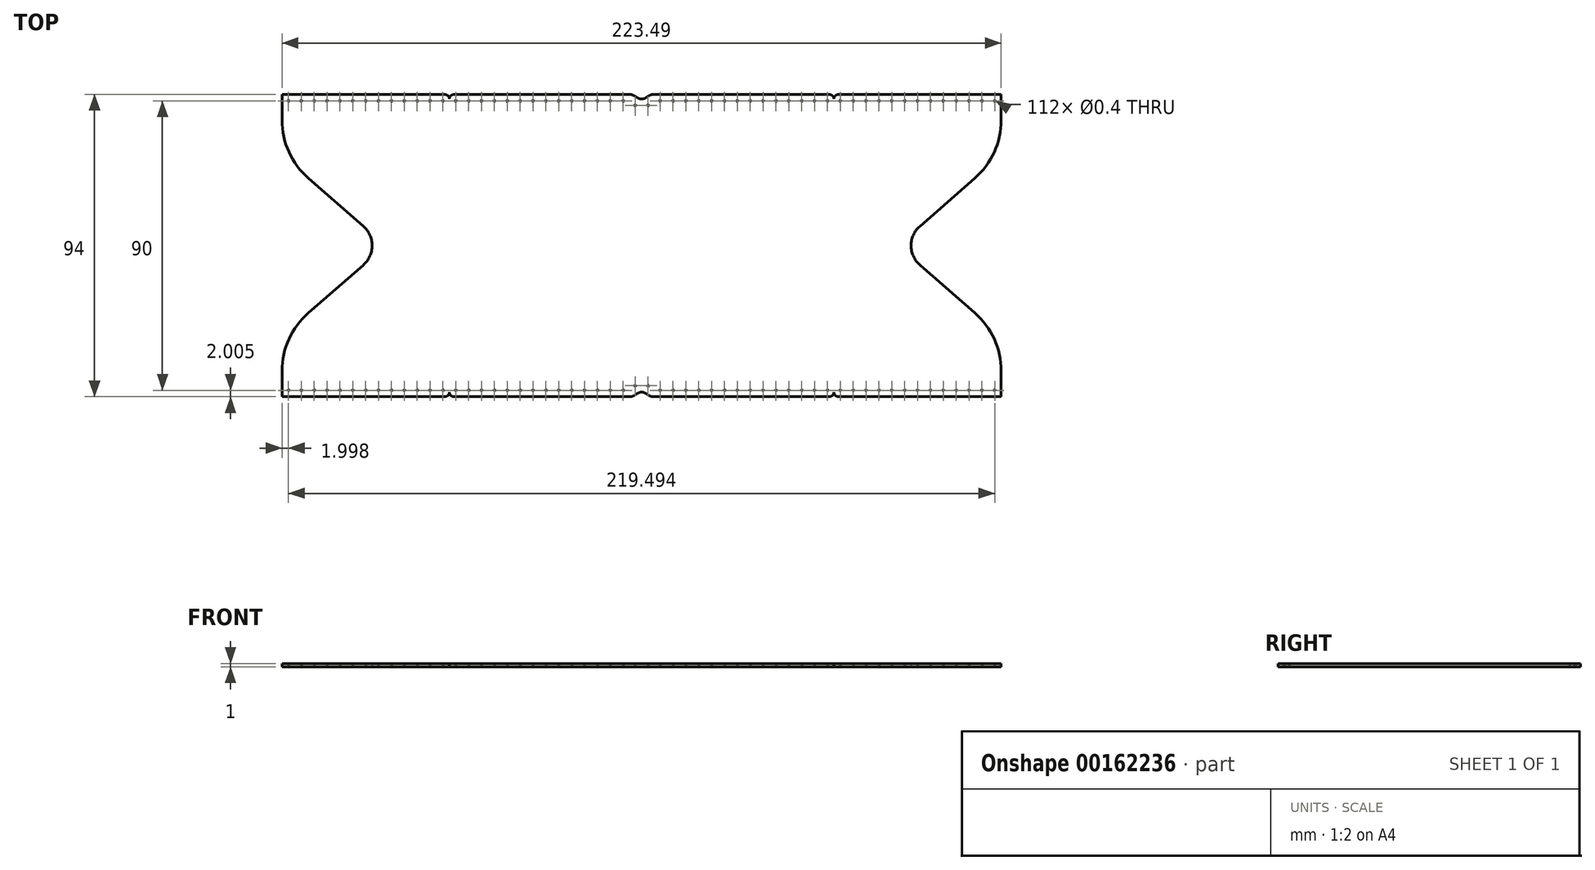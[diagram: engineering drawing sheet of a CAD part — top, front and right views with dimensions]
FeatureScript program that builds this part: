
annotation { "Feature Type Name" : "Feature", "Feature Type Description" : "" }
export const myFeature = defineFeature(function(context is Context, id is Id, definition is map)
    precondition{}
    {
        {
            var Q0;
            Q0=qCreatedBy(makeId("Top.planeOp"),FACE);
            var sketch = newSketch(context, id + "F0", { "sketchPlane" : qUnion([Q0])});
            skLineSegment(sketch, "E0", {"start": v(59.8, 51.12) * mm, "end": v(59.8, 5.52) * mm, "construction": true});
            skCircle(sketch, "E1.27.0.0", {"center": v(5.8, 50.52) * mm, "radius": 0.2 * mm});
            skLineSegment(sketch, "E2", {"start": v(86.53, 11.55) * mm, "end": v(103.58, 26.45) * mm});
            skArc(sketch, "E3", {"start": v(103.58, 26.45) * mm, "mid": v(109.64, 34.6) * mm, "end": v(111.8, 44.52) * mm});
            skArc(sketch, "E4", {"start": v(86.53, 11.55) * mm, "mid": v(84.5, 8.83) * mm, "end": v(83.8, 5.52) * mm});
            skLineSegment(sketch, "E5.trimOffspring", {"start": v(111.8, 44.52) * mm, "end": v(111.8, 52.52) * mm});
            skLineSegment(sketch, "E6.trimOffspring", {"start": v(3.65, 52.52) * mm, "end": v(58.4, 52.52) * mm});
            skCircle(sketch, "E7.1.0.0", {"center": v(9.8, 50.52) * mm, "radius": 0.2 * mm});
            skCircle(sketch, "E7.2.0.0", {"center": v(13.8, 50.52) * mm, "radius": 0.2 * mm});
            skCircle(sketch, "E7.3.0.0", {"center": v(17.8, 50.52) * mm, "radius": 0.2 * mm});
            skCircle(sketch, "E7.4.0.0", {"center": v(21.8, 50.52) * mm, "radius": 0.2 * mm});
            skCircle(sketch, "E7.5.0.0", {"center": v(25.8, 50.52) * mm, "radius": 0.2 * mm});
            skCircle(sketch, "E7.6.0.0", {"center": v(29.8, 50.52) * mm, "radius": 0.2 * mm});
            skCircle(sketch, "E7.7.0.0", {"center": v(33.8, 50.52) * mm, "radius": 0.2 * mm});
            skCircle(sketch, "E7.8.0.0", {"center": v(37.8, 50.52) * mm, "radius": 0.2 * mm});
            skCircle(sketch, "E7.9.0.0", {"center": v(41.8, 50.52) * mm, "radius": 0.2 * mm});
            skCircle(sketch, "E7.10.0.0", {"center": v(45.8, 50.52) * mm, "radius": 0.2 * mm});
            skCircle(sketch, "E7.11.0.0", {"center": v(49.8, 50.52) * mm, "radius": 0.2 * mm});
            skCircle(sketch, "E7.12.0.0", {"center": v(53.8, 50.52) * mm, "radius": 0.2 * mm});
            skCircle(sketch, "E7.13.0.0", {"center": v(57.8, 50.52) * mm, "radius": 0.2 * mm});
            skCircle(sketch, "E7.14.0.0", {"center": v(61.8, 50.52) * mm, "radius": 0.2 * mm});
            skCircle(sketch, "E7.15.0.0", {"center": v(65.8, 50.52) * mm, "radius": 0.2 * mm});
            skCircle(sketch, "E7.16.0.0", {"center": v(69.8, 50.52) * mm, "radius": 0.2 * mm});
            skCircle(sketch, "E7.17.0.0", {"center": v(73.8, 50.52) * mm, "radius": 0.2 * mm});
            skCircle(sketch, "E7.18.0.0", {"center": v(77.8, 50.52) * mm, "radius": 0.2 * mm});
            skCircle(sketch, "E7.19.0.0", {"center": v(81.8, 50.52) * mm, "radius": 0.2 * mm});
            skCircle(sketch, "E7.20.0.0", {"center": v(85.8, 50.52) * mm, "radius": 0.2 * mm});
            skCircle(sketch, "E7.21.0.0", {"center": v(89.8, 50.52) * mm, "radius": 0.2 * mm});
            skCircle(sketch, "E7.22.0.0", {"center": v(93.8, 50.52) * mm, "radius": 0.2 * mm});
            skCircle(sketch, "E7.23.0.0", {"center": v(97.8, 50.52) * mm, "radius": 0.2 * mm});
            skCircle(sketch, "E7.24.0.0", {"center": v(101.8, 50.52) * mm, "radius": 0.2 * mm});
            skCircle(sketch, "E7.25.0.0", {"center": v(105.8, 50.52) * mm, "radius": 0.2 * mm});
            skCircle(sketch, "E7.26.0.0", {"center": v(109.8, 50.52) * mm, "radius": 0.2 * mm});
            skLineSegment(sketch, "E7.direction1", {"start": v(5.8, 50.52) * mm, "end": v(9.8, 50.52) * mm, "construction": true});
            skArc(sketch, "E8", {"start": v(59.8, 51.12) * mm, "mid": v(59.38, 52.11) * mm, "end": v(58.4, 52.52) * mm});
            skArc(sketch, "E9", {"start": v(59.8, 51.12) * mm, "mid": v(60.2, 52.11) * mm, "end": v(61.2, 52.52) * mm});
            skLineSegment(sketch, "E10.trimOffspring", {"start": v(61.2, 52.52) * mm, "end": v(111.8, 52.52) * mm});
            skCircle(sketch, "E11", {"center": v(2.05, 49.12) * mm, "radius": 0.2 * mm});
            skFitSpline(sketch, "E12", {"points": [v(3.65, 52.52) * mm, v(1.85, 51.82) * mm, v(0.05, 51.12) * mm], "startDerivative": vector(-4.8, 0) * mm, "endDerivative": vector(-4.8, 0) * mm});
            skLineSegment(sketch, "E13", {"start": v(0.05, 5.52) * mm, "end": v(91.8, 5.52) * mm, "construction": true});
            skLineSegment(sketch, "E14", {"start": v(0.05, 5.52) * mm, "end": v(0.05, 51.12) * mm, "construction": true});
            skLineSegment(sketch, "E15", {"start": v(2.85, 52.52) * mm, "end": v(3.65, 52.52) * mm, "construction": true});
            skLineSegment(sketch, "E16", {"start": v(0.85, 51.12) * mm, "end": v(0.05, 51.12) * mm, "construction": true});
            skLineSegment(sketch, "E17.MirrorCS", {"start": v(0.85, -40.08) * mm, "end": v(0.05, -40.08) * mm, "construction": true});
            skLineSegment(sketch, "E18.MirrorCS", {"start": v(2.85, -41.48) * mm, "end": v(3.65, -41.48) * mm, "construction": true});
            skFitSpline(sketch, "E19.MirrorCS", {"points": [v(3.65, -41.48) * mm, v(1.85, -40.78) * mm, v(0.05, -40.08) * mm], "startDerivative": vector(-4.8, 0) * mm, "endDerivative": vector(-4.8, 0) * mm});
            skCircle(sketch, "E20.MirrorC", {"center": v(2.05, -38.08) * mm, "radius": 0.2 * mm});
            skLineSegment(sketch, "E21.MirrorCS", {"start": v(61.2, -41.48) * mm, "end": v(111.8, -41.48) * mm});
            skArc(sketch, "E22.MirrorCS", {"start": v(59.8, -40.08) * mm, "mid": v(60.2, -41.07) * mm, "end": v(61.2, -41.48) * mm});
            skArc(sketch, "E23.MirrorCS", {"start": v(59.8, -40.08) * mm, "mid": v(59.38, -41.07) * mm, "end": v(58.4, -41.48) * mm});
            skLineSegment(sketch, "E24.MirrorCS", {"start": v(59.8, -40.08) * mm, "end": v(59.8, 5.52) * mm, "construction": true});
            skLineSegment(sketch, "E25.MirrorCS", {"start": v(5.8, -39.48) * mm, "end": v(9.8, -39.48) * mm, "construction": true});
            skCircle(sketch, "E26.MirrorC", {"center": v(109.8, -39.48) * mm, "radius": 0.2 * mm});
            skCircle(sketch, "E27.MirrorC", {"center": v(105.8, -39.48) * mm, "radius": 0.2 * mm});
            skCircle(sketch, "E28.MirrorC", {"center": v(101.8, -39.48) * mm, "radius": 0.2 * mm});
            skCircle(sketch, "E29.MirrorC", {"center": v(97.8, -39.48) * mm, "radius": 0.2 * mm});
            skCircle(sketch, "E30.MirrorC", {"center": v(93.8, -39.48) * mm, "radius": 0.2 * mm});
            skCircle(sketch, "E31.MirrorC", {"center": v(89.8, -39.48) * mm, "radius": 0.2 * mm});
            skCircle(sketch, "E32.MirrorC", {"center": v(85.8, -39.48) * mm, "radius": 0.2 * mm});
            skCircle(sketch, "E33.MirrorC", {"center": v(81.8, -39.48) * mm, "radius": 0.2 * mm});
            skCircle(sketch, "E34.MirrorC", {"center": v(77.8, -39.48) * mm, "radius": 0.2 * mm});
            skCircle(sketch, "E35.MirrorC", {"center": v(73.8, -39.48) * mm, "radius": 0.2 * mm});
            skCircle(sketch, "E36.MirrorC", {"center": v(69.8, -39.48) * mm, "radius": 0.2 * mm});
            skCircle(sketch, "E37.MirrorC", {"center": v(65.8, -39.48) * mm, "radius": 0.2 * mm});
            skCircle(sketch, "E38.MirrorC", {"center": v(61.8, -39.48) * mm, "radius": 0.2 * mm});
            skCircle(sketch, "E39.MirrorC", {"center": v(57.8, -39.48) * mm, "radius": 0.2 * mm});
            skCircle(sketch, "E40.MirrorC", {"center": v(53.8, -39.48) * mm, "radius": 0.2 * mm});
            skCircle(sketch, "E41.MirrorC", {"center": v(49.8, -39.48) * mm, "radius": 0.2 * mm});
            skCircle(sketch, "E42.MirrorC", {"center": v(45.8, -39.48) * mm, "radius": 0.2 * mm});
            skCircle(sketch, "E43.MirrorC", {"center": v(41.8, -39.48) * mm, "radius": 0.2 * mm});
            skCircle(sketch, "E44.MirrorC", {"center": v(37.8, -39.48) * mm, "radius": 0.2 * mm});
            skCircle(sketch, "E45.MirrorC", {"center": v(33.8, -39.48) * mm, "radius": 0.2 * mm});
            skCircle(sketch, "E46.MirrorC", {"center": v(29.8, -39.48) * mm, "radius": 0.2 * mm});
            skCircle(sketch, "E47.MirrorC", {"center": v(25.8, -39.48) * mm, "radius": 0.2 * mm});
            skCircle(sketch, "E48.MirrorC", {"center": v(21.8, -39.48) * mm, "radius": 0.2 * mm});
            skCircle(sketch, "E49.MirrorC", {"center": v(17.8, -39.48) * mm, "radius": 0.2 * mm});
            skCircle(sketch, "E50.MirrorC", {"center": v(13.8, -39.48) * mm, "radius": 0.2 * mm});
            skCircle(sketch, "E51.MirrorC", {"center": v(9.8, -39.48) * mm, "radius": 0.2 * mm});
            skLineSegment(sketch, "E52.MirrorCS", {"start": v(3.65, -41.48) * mm, "end": v(58.4, -41.48) * mm});
            skLineSegment(sketch, "E53.MirrorCS", {"start": v(111.8, -33.48) * mm, "end": v(111.8, -41.48) * mm});
            skArc(sketch, "E54.MirrorCS", {"start": v(86.53, -0.5) * mm, "mid": v(84.5, 2.22) * mm, "end": v(83.8, 5.52) * mm});
            skArc(sketch, "E55.MirrorCS", {"start": v(103.58, -15.4) * mm, "mid": v(109.64, -23.55) * mm, "end": v(111.8, -33.48) * mm});
            skLineSegment(sketch, "E56.MirrorCS", {"start": v(86.53, -0.5) * mm, "end": v(103.58, -15.4) * mm});
            skCircle(sketch, "E57.MirrorC", {"center": v(5.8, -39.48) * mm, "radius": 0.2 * mm});
            skLineSegment(sketch, "E58.MirrorCS", {"start": v(-2.75, 52.52) * mm, "end": v(-3.55, 52.52) * mm, "construction": true});
            skFitSpline(sketch, "E59.MirrorCS", {"points": [v(-3.55, 52.52) * mm, v(-1.75, 51.82) * mm, v(0.05, 51.12) * mm], "startDerivative": vector(4.8, 0) * mm, "endDerivative": vector(4.8, 0) * mm});
            skArc(sketch, "E60.MirrorCS", {"start": v(-59.7, 51.12) * mm, "mid": v(-60.11, 52.11) * mm, "end": v(-61.1, 52.52) * mm});
            skLineSegment(sketch, "E61.MirrorCS", {"start": v(-0.75, 51.12) * mm, "end": v(0.05, 51.12) * mm, "construction": true});
            skLineSegment(sketch, "E62.MirrorCS", {"start": v(-2.75, -41.48) * mm, "end": v(-3.55, -41.48) * mm, "construction": true});
            skArc(sketch, "E63.MirrorCS", {"start": v(-59.7, 51.12) * mm, "mid": v(-59.3, 52.11) * mm, "end": v(-58.3, 52.52) * mm});
            skArc(sketch, "E64.MirrorCS", {"start": v(-59.7, -40.08) * mm, "mid": v(-59.3, -41.07) * mm, "end": v(-58.3, -41.48) * mm});
            skCircle(sketch, "E65.MirrorC", {"center": v(-57.7, -39.48) * mm, "radius": 0.2 * mm});
            skLineSegment(sketch, "E66.MirrorCS", {"start": v(-0.75, -40.08) * mm, "end": v(0.05, -40.08) * mm, "construction": true});
            skFitSpline(sketch, "E67.MirrorCS", {"points": [v(-3.55, -41.48) * mm, v(-1.75, -40.78) * mm, v(0.05, -40.08) * mm], "startDerivative": vector(4.8, 0) * mm, "endDerivative": vector(4.8, 0) * mm});
            skArc(sketch, "E68.MirrorCS", {"start": v(-59.7, -40.08) * mm, "mid": v(-60.11, -41.07) * mm, "end": v(-61.1, -41.48) * mm});
            skLineSegment(sketch, "E69.MirrorCS", {"start": v(-5.7, 50.52) * mm, "end": v(-9.7, 50.52) * mm, "construction": true});
            skCircle(sketch, "E70.MirrorC", {"center": v(-5.7, -39.48) * mm, "radius": 0.2 * mm});
            skCircle(sketch, "E71.MirrorC", {"center": v(-61.7, 50.52) * mm, "radius": 0.2 * mm});
            skCircle(sketch, "E72.MirrorC", {"center": v(-57.7, 50.52) * mm, "radius": 0.2 * mm});
            skCircle(sketch, "E73.MirrorC", {"center": v(-9.7, -39.48) * mm, "radius": 0.2 * mm});
            skCircle(sketch, "E74.MirrorC", {"center": v(-9.7, 50.52) * mm, "radius": 0.2 * mm});
            skCircle(sketch, "E75.MirrorC", {"center": v(-5.7, 50.52) * mm, "radius": 0.2 * mm});
            skLineSegment(sketch, "E76.MirrorCS", {"start": v(-5.7, -39.48) * mm, "end": v(-9.7, -39.48) * mm, "construction": true});
            skCircle(sketch, "E77.MirrorC", {"center": v(-1.95, 49.12) * mm, "radius": 0.2 * mm});
            skCircle(sketch, "E78.MirrorC", {"center": v(-37.7, -39.48) * mm, "radius": 0.2 * mm});
            skCircle(sketch, "E79.MirrorC", {"center": v(-49.7, -39.48) * mm, "radius": 0.2 * mm});
            skCircle(sketch, "E80.MirrorC", {"center": v(-65.7, -39.48) * mm, "radius": 0.2 * mm});
            skCircle(sketch, "E81.MirrorC", {"center": v(-105.7, -39.48) * mm, "radius": 0.2 * mm});
            skCircle(sketch, "E82.MirrorC", {"center": v(-53.7, 50.52) * mm, "radius": 0.2 * mm});
            skCircle(sketch, "E83.MirrorC", {"center": v(-21.7, 50.52) * mm, "radius": 0.2 * mm});
            skCircle(sketch, "E84.MirrorC", {"center": v(-21.7, -39.48) * mm, "radius": 0.2 * mm});
            skCircle(sketch, "E85.MirrorC", {"center": v(-73.7, -39.48) * mm, "radius": 0.2 * mm});
            skCircle(sketch, "E86.MirrorC", {"center": v(-29.7, 50.52) * mm, "radius": 0.2 * mm});
            skCircle(sketch, "E87.MirrorC", {"center": v(-17.7, -39.48) * mm, "radius": 0.2 * mm});
            skCircle(sketch, "E88.MirrorC", {"center": v(-105.7, 50.52) * mm, "radius": 0.2 * mm});
            skCircle(sketch, "E89.MirrorC", {"center": v(-69.7, 50.52) * mm, "radius": 0.2 * mm});
            skCircle(sketch, "E90.MirrorC", {"center": v(-29.7, -39.48) * mm, "radius": 0.2 * mm});
            skCircle(sketch, "E91.MirrorC", {"center": v(-37.7, 50.52) * mm, "radius": 0.2 * mm});
            skCircle(sketch, "E92.MirrorC", {"center": v(-13.7, -39.48) * mm, "radius": 0.2 * mm});
            skCircle(sketch, "E93.MirrorC", {"center": v(-109.7, 50.52) * mm, "radius": 0.2 * mm});
            skCircle(sketch, "E94.MirrorC", {"center": v(-101.7, 50.52) * mm, "radius": 0.2 * mm});
            skCircle(sketch, "E95.MirrorC", {"center": v(-33.7, 50.52) * mm, "radius": 0.2 * mm});
            skCircle(sketch, "E96.MirrorC", {"center": v(-97.7, -39.48) * mm, "radius": 0.2 * mm});
            skCircle(sketch, "E97.MirrorC", {"center": v(-41.7, 50.52) * mm, "radius": 0.2 * mm});
            skCircle(sketch, "E98.MirrorC", {"center": v(-33.7, -39.48) * mm, "radius": 0.2 * mm});
            skCircle(sketch, "E99.MirrorC", {"center": v(-109.7, -39.48) * mm, "radius": 0.2 * mm});
            skCircle(sketch, "E100.MirrorC", {"center": v(-69.7, -39.48) * mm, "radius": 0.2 * mm});
            skCircle(sketch, "E101.MirrorC", {"center": v(-53.7, -39.48) * mm, "radius": 0.2 * mm});
            skCircle(sketch, "E102.MirrorC", {"center": v(-93.7, 50.52) * mm, "radius": 0.2 * mm});
            skCircle(sketch, "E103.MirrorC", {"center": v(-49.7, 50.52) * mm, "radius": 0.2 * mm});
            skCircle(sketch, "E104.MirrorC", {"center": v(-85.7, 50.52) * mm, "radius": 0.2 * mm});
            skCircle(sketch, "E105.MirrorC", {"center": v(-77.7, -39.48) * mm, "radius": 0.2 * mm});
            skCircle(sketch, "E106.MirrorC", {"center": v(-45.7, -39.48) * mm, "radius": 0.2 * mm});
            skCircle(sketch, "E107.MirrorC", {"center": v(-25.7, 50.52) * mm, "radius": 0.2 * mm});
            skCircle(sketch, "E108.MirrorC", {"center": v(-73.7, 50.52) * mm, "radius": 0.2 * mm});
            skCircle(sketch, "E109.MirrorC", {"center": v(-93.7, -39.48) * mm, "radius": 0.2 * mm});
            skCircle(sketch, "E110.MirrorC", {"center": v(-101.7, -39.48) * mm, "radius": 0.2 * mm});
            skCircle(sketch, "E111.MirrorC", {"center": v(-81.7, -39.48) * mm, "radius": 0.2 * mm});
            skCircle(sketch, "E112.MirrorC", {"center": v(-97.7, 50.52) * mm, "radius": 0.2 * mm});
            skCircle(sketch, "E113.MirrorC", {"center": v(-1.95, -38.08) * mm, "radius": 0.2 * mm});
            skCircle(sketch, "E114.MirrorC", {"center": v(-65.7, 50.52) * mm, "radius": 0.2 * mm});
            skCircle(sketch, "E115.MirrorC", {"center": v(-77.7, 50.52) * mm, "radius": 0.2 * mm});
            skCircle(sketch, "E116.MirrorC", {"center": v(-81.7, 50.52) * mm, "radius": 0.2 * mm});
            skCircle(sketch, "E117.MirrorC", {"center": v(-85.7, -39.48) * mm, "radius": 0.2 * mm});
            skCircle(sketch, "E118.MirrorC", {"center": v(-41.7, -39.48) * mm, "radius": 0.2 * mm});
            skCircle(sketch, "E119.MirrorC", {"center": v(-89.7, -39.48) * mm, "radius": 0.2 * mm});
            skCircle(sketch, "E120.MirrorC", {"center": v(-61.7, -39.48) * mm, "radius": 0.2 * mm});
            skCircle(sketch, "E121.MirrorC", {"center": v(-89.7, 50.52) * mm, "radius": 0.2 * mm});
            skCircle(sketch, "E122.MirrorC", {"center": v(-45.7, 50.52) * mm, "radius": 0.2 * mm});
            skCircle(sketch, "E123.MirrorC", {"center": v(-13.7, 50.52) * mm, "radius": 0.2 * mm});
            skCircle(sketch, "E124.MirrorC", {"center": v(-25.7, -39.48) * mm, "radius": 0.2 * mm});
            skCircle(sketch, "E125.MirrorC", {"center": v(-17.7, 50.52) * mm, "radius": 0.2 * mm});
            skLineSegment(sketch, "E126.MirrorCS", {"start": v(0.05, 5.52) * mm, "end": v(-91.7, 5.52) * mm, "construction": true});
            skLineSegment(sketch, "E127.MirrorCS", {"start": v(-61.1, 52.52) * mm, "end": v(-111.7, 52.52) * mm});
            skLineSegment(sketch, "E128.MirrorCS", {"start": v(-59.7, 51.12) * mm, "end": v(-59.7, 5.52) * mm, "construction": true});
            skLineSegment(sketch, "E129.MirrorCS", {"start": v(-59.7, -40.08) * mm, "end": v(-59.7, 5.52) * mm, "construction": true});
            skLineSegment(sketch, "E130.MirrorCS", {"start": v(-111.7, 44.52) * mm, "end": v(-111.7, 52.52) * mm});
            skLineSegment(sketch, "E131.MirrorCS", {"start": v(-61.1, -41.48) * mm, "end": v(-111.7, -41.48) * mm});
            skArc(sketch, "E132.MirrorCS", {"start": v(-86.44, 11.55) * mm, "mid": v(-84.42, 8.83) * mm, "end": v(-83.7, 5.52) * mm});
            skLineSegment(sketch, "E133.MirrorCS", {"start": v(-3.55, -41.48) * mm, "end": v(-58.3, -41.48) * mm});
            skArc(sketch, "E134.MirrorCS", {"start": v(-86.44, -0.5) * mm, "mid": v(-84.42, 2.22) * mm, "end": v(-83.7, 5.52) * mm});
            skLineSegment(sketch, "E135.MirrorCS", {"start": v(-86.44, 11.55) * mm, "end": v(-103.5, 26.45) * mm});
            skLineSegment(sketch, "E136.MirrorCS", {"start": v(-3.55, 52.52) * mm, "end": v(-58.3, 52.52) * mm});
            skArc(sketch, "E137.MirrorCS", {"start": v(-103.5, -15.4) * mm, "mid": v(-109.55, -23.55) * mm, "end": v(-111.7, -33.48) * mm});
            skLineSegment(sketch, "E138.MirrorCS", {"start": v(-111.7, -33.48) * mm, "end": v(-111.7, -41.48) * mm});
            skLineSegment(sketch, "E139.MirrorCS", {"start": v(-86.44, -0.5) * mm, "end": v(-103.5, -15.4) * mm});
            skArc(sketch, "E140.MirrorCS", {"start": v(-103.5, 26.45) * mm, "mid": v(-109.55, 34.6) * mm, "end": v(-111.7, 44.52) * mm});
            skSolve(sketch);
        }
        {
            var Q0;
            Q0 = qSketchRegion(id + "F0", true);
            extrude(context, id + "F1", {"entities" : qUnion([Q0]), "depth" : 1 * mm});
        }
    });
